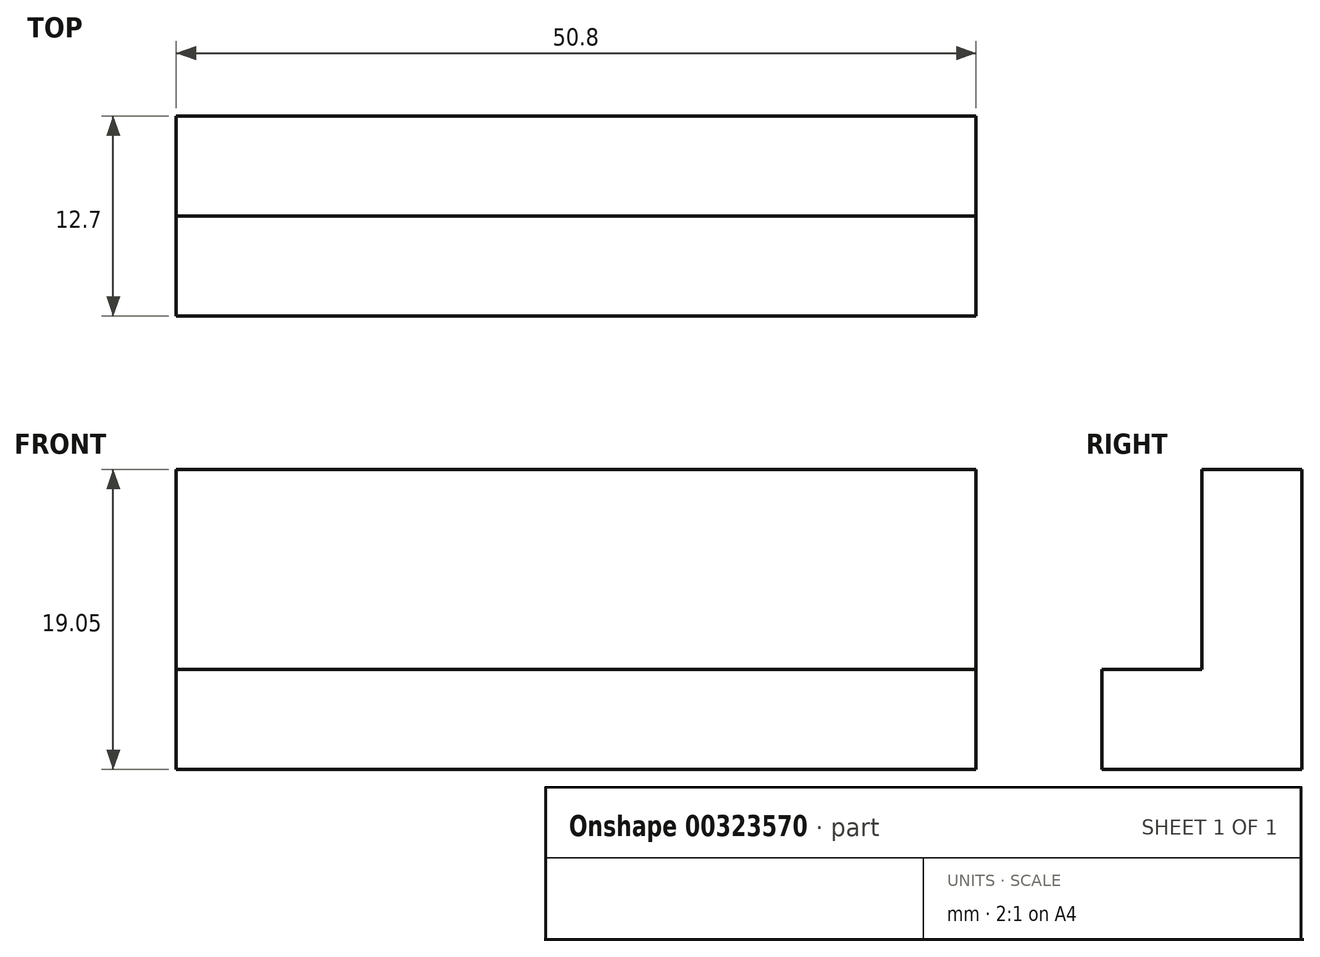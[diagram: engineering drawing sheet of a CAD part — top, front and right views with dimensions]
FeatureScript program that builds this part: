
annotation { "Feature Type Name" : "Feature", "Feature Type Description" : "" }
export const myFeature = defineFeature(function(context is Context, id is Id, definition is map)
    precondition{}
    {
        {
            var Q0;
            Q0=qCreatedBy(makeId("Top.planeOp"),FACE);
            var sketch = newSketch(context, id + "F0", { "sketchPlane" : qUnion([Q0])});
            skLineSegment(sketch, "E0.bottom", {"start": v(0, 0) * mm, "end": v(50.8, 0) * mm});
            skLineSegment(sketch, "E0.top", {"start": v(0, 12.7) * mm, "end": v(50.8, 12.7) * mm});
            skLineSegment(sketch, "E0.left", {"start": v(0, 0) * mm, "end": v(0, 12.7) * mm});
            skLineSegment(sketch, "E0.right", {"start": v(50.8, 0) * mm, "end": v(50.8, 12.7) * mm});
            skSolve(sketch);
        }
        {
            var Q0;
            Q0=makeQuery(id+"F0.imprint","IMPRINT",FACE,{"disambiguationData":[TD([[makeQuery(id+"F0.imprint","IMPRINT",EDGE,{"derivedFrom":sQuery(id+"F0.wireOp",EDGE,"E0.bottom")}),1.0]])]});
            extrude(context, id + "F1", {"entities" : qUnion([Q0]), "depth" : 6.35 * mm});
        }
        {
            var Q0;
            Q0=makeQuery(id+"F1.opExtrude","CAP_FACE",FACE,{"disambiguationData":[OSD([sQuery(id+"F0.wireOp",EDGE,"E0.bottom"),sQuery(id+"F0.wireOp",EDGE,"E0.top"),sQuery(id+"F0.wireOp",EDGE,"E0.left"),sQuery(id+"F0.wireOp",EDGE,"E0.right")])],"isStart":false});
            var sketch = newSketch(context, id + "F2", { "sketchPlane" : qUnion([Q0])});
            skLineSegment(sketch, "E1.bottom", {"start": v(0, 12.7) * mm, "end": v(50.8, 12.7) * mm});
            skLineSegment(sketch, "E1.top", {"start": v(0, 6.35) * mm, "end": v(50.8, 6.35) * mm});
            skLineSegment(sketch, "E1.left", {"start": v(0, 12.7) * mm, "end": v(0, 6.35) * mm});
            skLineSegment(sketch, "E1.right", {"start": v(50.8, 12.7) * mm, "end": v(50.8, 6.35) * mm});
            skLineSegment(sketch, "E2", {"start": v(25.4, 6.35) * mm, "end": v(31.75, 6.35) * mm});
            skLineSegment(sketch, "E3", {"start": v(31.75, 6.35) * mm, "end": v(31.75, 0) * mm});
            skLineSegment(sketch, "E4", {"start": v(19.05, 0) * mm, "end": v(31.75, 0) * mm});
            skLineSegment(sketch, "E5", {"start": v(19.05, 0) * mm, "end": v(19.05, 6.35) * mm});
            skSolve(sketch);
        }
        {
            var Q0;
            Q0=makeQuery(id+"F2.imprint","IMPRINT",FACE,{"disambiguationData":[TD([[makeQuery(id+"F2.imprint","IMPRINT",EDGE,{"derivedFrom":sQuery(id+"F2.wireOp",EDGE,"E1.bottom")}),-1.0]])]});
            extrude(context, id + "F3", {"entities" : qUnion([Q0]), "operationType" : NewBodyOperationType.ADD, "depth" : 12.7 * mm});
        }
    });
